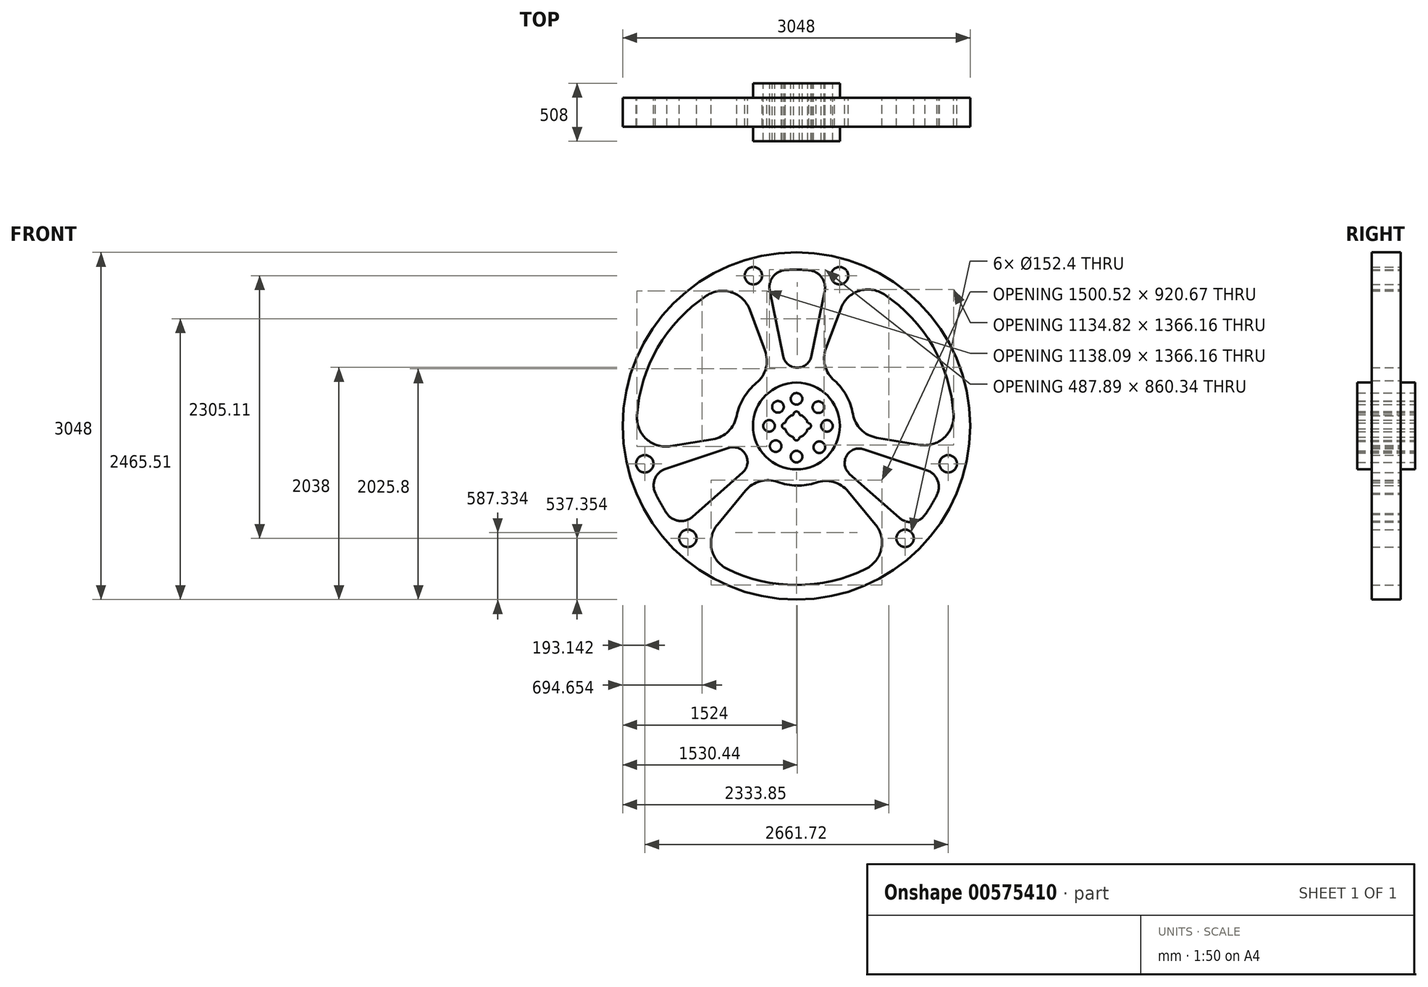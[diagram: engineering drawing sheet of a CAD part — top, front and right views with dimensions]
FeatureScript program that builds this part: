
annotation { "Feature Type Name" : "Feature", "Feature Type Description" : "" }
export const myFeature = defineFeature(function(context is Context, id is Id, definition is map)
    precondition{}
    {
        {
            var Q0;
            Q0=qCreatedBy(makeId("Front.planeOp"),FACE);
            var sketch = newSketch(context, id + "F0", { "sketchPlane" : qUnion([Q0])});
            skCircle(sketch, "E0", {"center": v(0, 0) * mm, "radius": 1524 * mm});
            skArc(sketch, "E1", {"start": v(-609.08, -1254.35) * mm, "mid": v(0, -1397) * mm, "end": v(609.08, -1254.35) * mm});
            skArc(sketch, "E2", {"start": v(-164.75, -491.47) * mm, "mid": v(-318.5, -485.04) * mm, "end": v(-447.73, -568.55) * mm});
            skArc(sketch, "E3", {"start": v(-692.28, -865.2) * mm, "mid": v(-744.67, -1079.87) * mm, "end": v(-609.08, -1254.35) * mm});
            skArc(sketch, "E4", {"start": v(453.69, -575.77) * mm, "mid": v(324.44, -492.26) * mm, "end": v(170.7, -498.7) * mm});
            skArc(sketch, "E5", {"start": v(609.08, -1254.35) * mm, "mid": v(744.67, -1079.87) * mm, "end": v(692.28, -865.2) * mm});
            skLineSegment(sketch, "E6.trimOffspring", {"start": v(-447.73, -568.55) * mm, "end": v(-692.28, -865.2) * mm});
            skLineSegment(sketch, "E7.trimOffspring", {"start": v(453.69, -575.77) * mm, "end": v(692.28, -865.2) * mm});
            skArc(sketch, "E8.trimOffspring", {"start": v(-164.75, -491.47) * mm, "mid": v(2.36, -523.58) * mm, "end": v(170.7, -498.7) * mm});
            skArc(sketch, "E9.1.0", {"start": v(494.42, 103.95) * mm, "mid": v(565.72, -32.42) * mm, "end": v(702.66, -102.59) * mm});
            skArc(sketch, "E9.1.1", {"start": v(494.42, 103.95) * mm, "mid": v(438.67, 264.72) * mm, "end": v(332.95, 398.06) * mm});
            skArc(sketch, "E9.1.2", {"start": v(258.2, 681.67) * mm, "mid": v(250.5, 528) * mm, "end": v(332.95, 398.06) * mm});
            skLineSegment(sketch, "E9.1.3", {"start": v(258.2, 681.67) * mm, "end": v(389.57, 1033.02) * mm});
            skArc(sketch, "E9.1.4", {"start": v(768.18, 1155.54) * mm, "mid": v(549.28, 1185.73) * mm, "end": v(389.57, 1033.02) * mm});
            skArc(sketch, "E9.1.5", {"start": v(1081.84, -166.04) * mm, "mid": v(1293.95, -104.08) * mm, "end": v(1377.25, 100.58) * mm});
            skLineSegment(sketch, "E9.1.6", {"start": v(702.66, -102.59) * mm, "end": v(1081.84, -166.04) * mm});
            skArc(sketch, "E9.1.7", {"start": v(1377.25, 100.58) * mm, "mid": v(1196.26, 699.39) * mm, "end": v(768.18, 1155.54) * mm});
            skArc(sketch, "E9.2.0", {"start": v(-350.81, 377.1) * mm, "mid": v(-268.37, 507.02) * mm, "end": v(-276.07, 660.7) * mm});
            skArc(sketch, "E9.2.1", {"start": v(-350.81, 377.1) * mm, "mid": v(-462.17, 248.42) * mm, "end": v(-524.79, 90.2) * mm});
            skArc(sketch, "E9.2.2", {"start": v(-733.03, -116.34) * mm, "mid": v(-596.09, -46.16) * mm, "end": v(-524.79, 90.2) * mm});
            skLineSegment(sketch, "E9.2.3", {"start": v(-733.03, -116.34) * mm, "end": v(-1102.98, -178.25) * mm});
            skArc(sketch, "E9.2.4", {"start": v(-1398.4, 88.38) * mm, "mid": v(-1315.09, -116.29) * mm, "end": v(-1102.98, -178.25) * mm});
            skArc(sketch, "E9.2.5", {"start": v(-410.7, 1020.81) * mm, "mid": v(-570.42, 1173.52) * mm, "end": v(-789.32, 1143.33) * mm});
            skLineSegment(sketch, "E9.2.6", {"start": v(-276.07, 660.7) * mm, "end": v(-410.7, 1020.81) * mm});
            skArc(sketch, "E9.2.7", {"start": v(-789.32, 1143.33) * mm, "mid": v(-1217.4, 687.18) * mm, "end": v(-1398.4, 88.38) * mm});
            skPoint(sketch, "E10.endSnap0", {"position": v(-268.37, 507.02) * mm});
            skArc(sketch, "E11", {"start": v(-96.6, 1369.03) * mm, "mid": v(-206.68, 1308.98) * mm, "end": v(-234.46, 1186.68) * mm});
            skArc(sketch, "E12", {"start": v(247.34, 1184.07) * mm, "mid": v(219.57, 1306.36) * mm, "end": v(109.48, 1366.42) * mm});
            skArc(sketch, "E13", {"start": v(-117.74, 613.02) * mm, "mid": v(6.7, 511.34) * mm, "end": v(131.16, 613.02) * mm});
            skArc(sketch, "E14.trimOffspring", {"start": v(109.48, 1366.42) * mm, "mid": v(6.5, 1371.6) * mm, "end": v(-96.6, 1369.03) * mm});
            skLineSegment(sketch, "E15.trimOffspring", {"start": v(131.16, 613.02) * mm, "end": v(247.34, 1184.07) * mm});
            skLineSegment(sketch, "E16.trimOffspring", {"start": v(-117.74, 613.02) * mm, "end": v(-234.46, 1186.68) * mm});
            skCircle(sketch, "E17", {"center": v(378.06, 1318.47) * mm, "radius": 76.2 * mm});
            skCircle(sketch, "E18", {"center": v(-378.06, 1318.47) * mm, "radius": 76.2 * mm});
            skLineSegment(sketch, "E19.1.0", {"start": v(-596.47, -192.93) * mm, "end": v(-1149.1, -377.83) * mm});
            skArc(sketch, "E19.1.1", {"start": v(-1149.1, -377.83) * mm, "mid": v(-1241.12, -463.03) * mm, "end": v(-1238.1, -588.4) * mm});
            skArc(sketch, "E19.1.2", {"start": v(-1238.1, -588.4) * mm, "mid": v(-1191.09, -680.18) * mm, "end": v(-1137.32, -768.17) * mm});
            skArc(sketch, "E19.1.3", {"start": v(-1137.32, -768.17) * mm, "mid": v(-1030.27, -833.48) * mm, "end": v(-910.47, -796.39) * mm});
            skLineSegment(sketch, "E19.1.4", {"start": v(-472.02, -408.48) * mm, "end": v(-910.47, -796.39) * mm});
            skArc(sketch, "E19.1.5", {"start": v(-472.02, -408.48) * mm, "mid": v(-446.19, -249.86) * mm, "end": v(-596.47, -192.93) * mm});
            skCircle(sketch, "E19.1.6", {"center": v(-1330.86, -331.82) * mm, "radius": 76.2 * mm});
            skCircle(sketch, "E19.1.7", {"center": v(-952.8, -986.65) * mm, "radius": 76.2 * mm});
            skLineSegment(sketch, "E19.2.0", {"start": v(465.31, -420.1) * mm, "end": v(901.76, -806.24) * mm});
            skArc(sketch, "E19.2.1", {"start": v(901.76, -806.24) * mm, "mid": v(1021.56, -843.33) * mm, "end": v(1128.62, -778.02) * mm});
            skArc(sketch, "E19.2.2", {"start": v(1128.62, -778.02) * mm, "mid": v(1184.6, -691.42) * mm, "end": v(1233.91, -600.87) * mm});
            skArc(sketch, "E19.2.3", {"start": v(1233.91, -600.87) * mm, "mid": v(1236.95, -475.5) * mm, "end": v(1144.93, -390.3) * mm});
            skLineSegment(sketch, "E19.2.4", {"start": v(589.77, -204.54) * mm, "end": v(1144.93, -390.3) * mm});
            skArc(sketch, "E19.2.5", {"start": v(589.77, -204.54) * mm, "mid": v(439.48, -261.48) * mm, "end": v(465.31, -420.1) * mm});
            skCircle(sketch, "E19.2.6", {"center": v(952.8, -986.65) * mm, "radius": 76.2 * mm});
            skCircle(sketch, "E19.2.7", {"center": v(1330.86, -331.82) * mm, "radius": 76.2 * mm});
            skLineSegment(sketch, "E20.trimOffspring", {"start": v(-357.06, 1245.22) * mm, "end": v(-378.06, 1318.47) * mm});
            skLineSegment(sketch, "E21.trimOffspring", {"start": v(357.06, 1245.22) * mm, "end": v(378.06, 1318.47) * mm});
            skArc(sketch, "E22", {"start": v(-25.2, 98.43) * mm, "mid": v(-71.84, 71.84) * mm, "end": v(-98.43, 25.2) * mm});
            skArc(sketch, "E23", {"start": v(25.2, 98.42) * mm, "mid": v(0, 127) * mm, "end": v(-25.2, 98.43) * mm});
            skArc(sketch, "E24", {"start": v(98.42, -25.2) * mm, "mid": v(127, 0) * mm, "end": v(98.43, 25.2) * mm});
            skArc(sketch, "E25", {"start": v(-25.2, -98.43) * mm, "mid": v(0, -127) * mm, "end": v(25.2, -98.43) * mm});
            skArc(sketch, "E26", {"start": v(-98.43, 25.2) * mm, "mid": v(-127, 0) * mm, "end": v(-98.43, -25.2) * mm});
            skArc(sketch, "E27.trimOffspring", {"start": v(98.43, 25.2) * mm, "mid": v(71.84, 71.84) * mm, "end": v(25.2, 98.42) * mm});
            skArc(sketch, "E28.trimOffspring", {"start": v(25.2, -98.43) * mm, "mid": v(71.84, -71.84) * mm, "end": v(98.43, -25.2) * mm});
            skArc(sketch, "E29.trimOffspring", {"start": v(-98.42, -25.2) * mm, "mid": v(-71.84, -71.84) * mm, "end": v(-25.2, -98.43) * mm});
            skCircle(sketch, "E30", {"center": v(-240.22, 0) * mm, "radius": 50.8 * mm});
            skCircle(sketch, "E31", {"center": v(266.8, 0) * mm, "radius": 50.8 * mm});
            skCircle(sketch, "E32", {"center": v(0, -269.35) * mm, "radius": 50.8 * mm});
            skCircle(sketch, "E33", {"center": v(0, 237.96) * mm, "radius": 50.8 * mm});
            skCircle(sketch, "E34", {"center": v(192.09, 164.72) * mm, "radius": 50.8 * mm});
            skCircle(sketch, "E35", {"center": v(200.82, -187) * mm, "radius": 50.8 * mm});
            skCircle(sketch, "E36", {"center": v(-182.43, -177.58) * mm, "radius": 50.8 * mm});
            skCircle(sketch, "E37", {"center": v(-162.24, 167.89) * mm, "radius": 50.8 * mm});
            skCircle(sketch, "E38", {"center": v(0, 0) * mm, "radius": 381 * mm});
            skSolve(sketch);
        }
        {
            var Q0;
            Q0=makeQuery(id+"F0.imprint","IMPRINT",FACE,{"disambiguationData":[TD([[makeQuery(id+"F0.imprint","IMPRINT",EDGE,{"derivedFrom":sQuery(id+"F0.wireOp",EDGE,"E0")}),1.0]])]});
            extrude(context, id + "F1", {"entities" : qUnion([Q0]), "depth" : 254 * mm, "offsetDistance" : 25.4 * mm, "symmetric" : true});
        }
        {
            var Q0;
            Q0=makeQuery(id+"F0.imprint","IMPRINT",FACE,{"disambiguationData":[TD([[makeQuery(id+"F0.imprint","IMPRINT",EDGE,{"derivedFrom":sQuery(id+"F0.wireOp",EDGE,"E22")}),-1.0]])]});
            extrude(context, id + "F2", {"entities" : qUnion([Q0]), "operationType" : NewBodyOperationType.ADD, "depth" : 508 * mm, "offsetDistance" : 25.4 * mm, "symmetric" : true});
        }
    });
